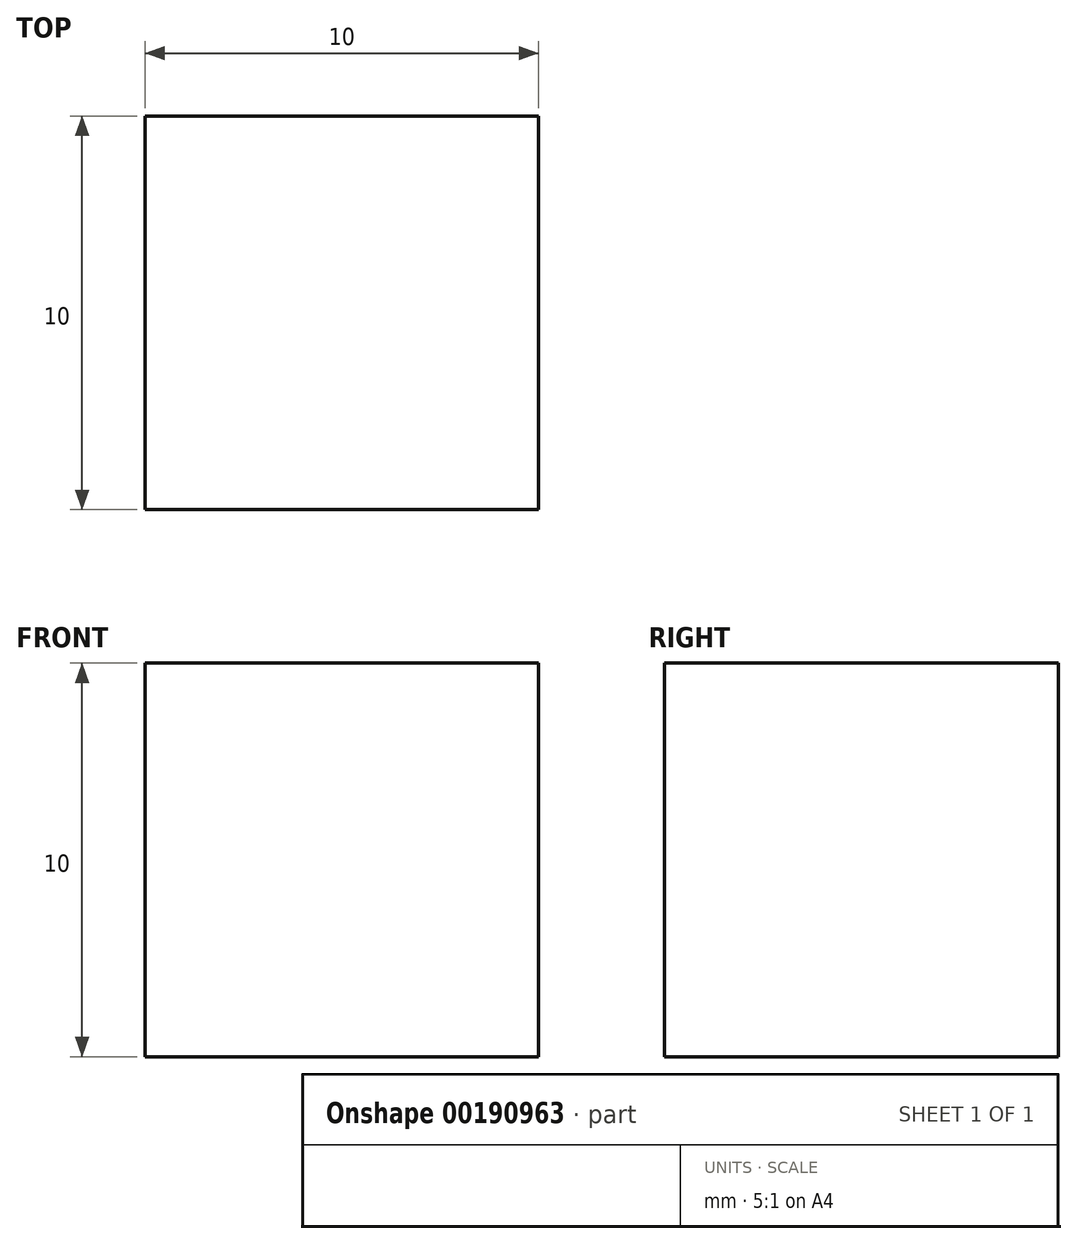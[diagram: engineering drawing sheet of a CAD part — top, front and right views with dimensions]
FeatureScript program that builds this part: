
annotation { "Feature Type Name" : "Feature", "Feature Type Description" : "" }
export const myFeature = defineFeature(function(context is Context, id is Id, definition is map)
    precondition{}
    {
        {
            var Q0;
            Q0=qCreatedBy(makeId("Front.planeOp"),FACE);
            var sketch = newSketch(context, id + "F0", { "sketchPlane" : qUnion([Q0])});
            skLineSegment(sketch, "E0.bottom", {"start": v(0, 0) * mm, "end": v(10, 0) * mm});
            skLineSegment(sketch, "E0.top", {"start": v(0, 10) * mm, "end": v(10, 10) * mm});
            skLineSegment(sketch, "E0.left", {"start": v(0, 0) * mm, "end": v(0, 10) * mm});
            skLineSegment(sketch, "E0.right", {"start": v(10, 0) * mm, "end": v(10, 10) * mm});
            skSolve(sketch);
        }
        {
            var Q0;
            Q0 = qSketchRegion(id + "F0", true);
            extrude(context, id + "F1", {"entities" : qUnion([Q0]), "depth" : 10 * mm, "offsetDistance" : 25 * mm});
        }
    });
